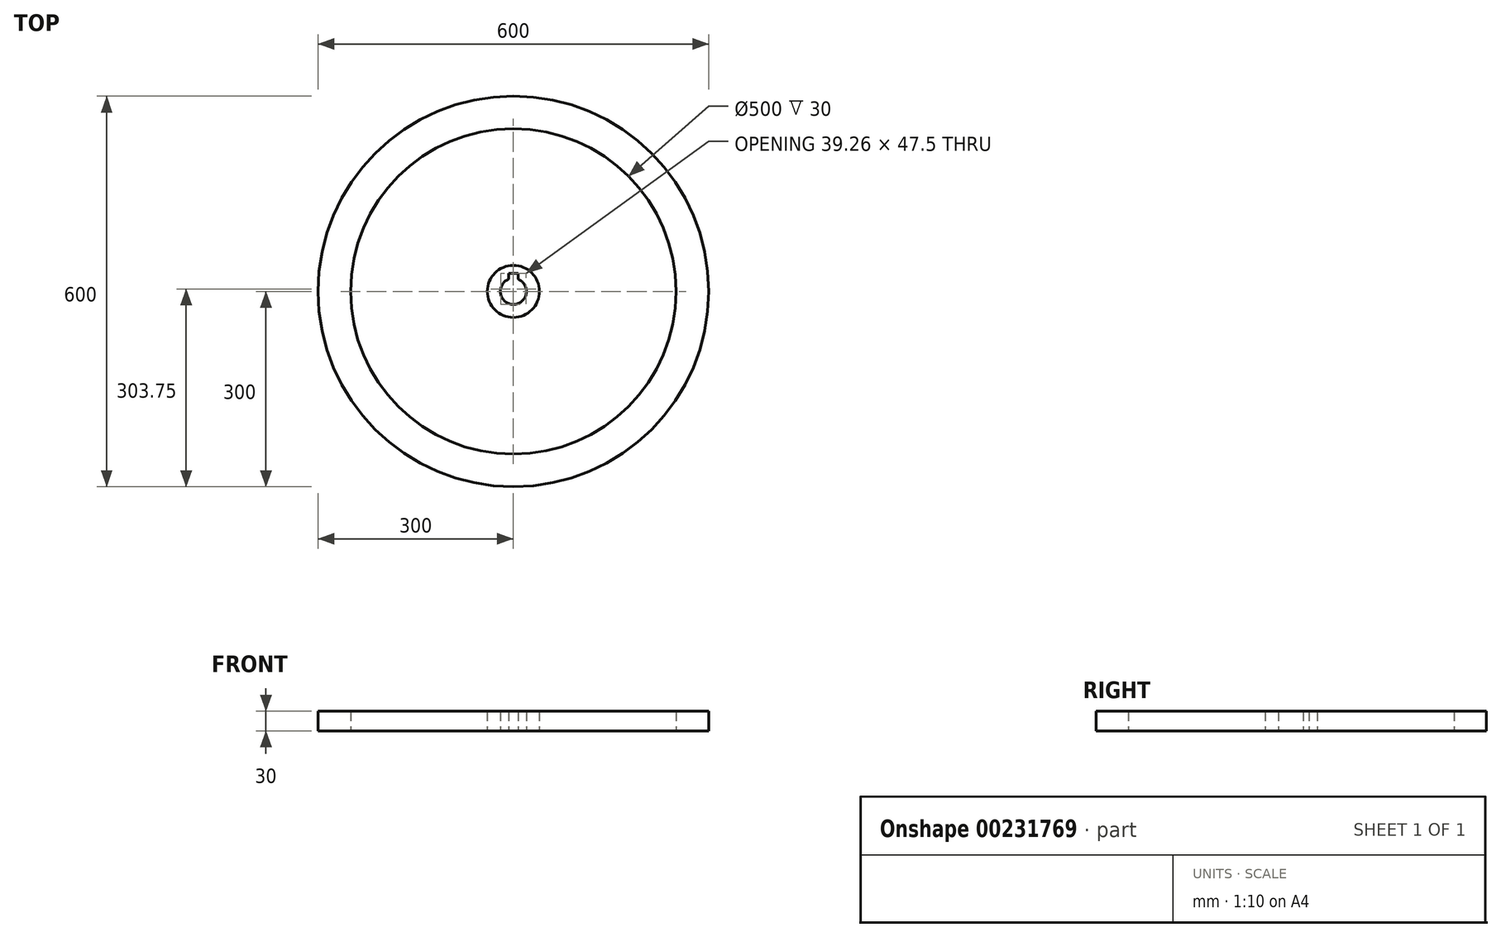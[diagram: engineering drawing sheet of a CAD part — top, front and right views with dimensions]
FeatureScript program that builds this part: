
annotation { "Feature Type Name" : "Feature", "Feature Type Description" : "" }
export const myFeature = defineFeature(function(context is Context, id is Id, definition is map)
    precondition{}
    {
        {
            var Q0;
            Q0=qCreatedBy(makeId("Top.planeOp"),FACE);
            var sketch = newSketch(context, id + "F0", { "sketchPlane" : qUnion([Q0])});
            skArc(sketch, "E0", {"start": v(-7.5, 18.54) * mm, "mid": v(0, -20) * mm, "end": v(7.5, 18.54) * mm});
            skLineSegment(sketch, "E1", {"start": v(-7.5, 18.54) * mm, "end": v(-7.5, 27.5) * mm});
            skLineSegment(sketch, "E2", {"start": v(-7.5, 27.5) * mm, "end": v(7.5, 27.5) * mm});
            skLineSegment(sketch, "E3", {"start": v(7.5, 27.5) * mm, "end": v(7.5, 18.54) * mm});
            skCircle(sketch, "E4", {"center": v(0, 0) * mm, "radius": 40 * mm});
            skCircle(sketch, "E5", {"center": v(0, 0) * mm, "radius": 250 * mm});
            skCircle(sketch, "E6", {"center": v(0, 0) * mm, "radius": 300 * mm});
            skSolve(sketch);
        }
        {
            var Q0;
            Q0=makeQuery(id+"F0.imprint","IMPRINT",FACE,{"disambiguationData":[TD([[makeQuery(id+"F0.imprint","IMPRINT",EDGE,{"derivedFrom":sQuery(id+"F0.wireOp",EDGE,"E0")}),-1.0]])]});
            var Q1;
            Q1=makeQuery(id+"F0.imprint","IMPRINT",FACE,{"disambiguationData":[TD([[makeQuery(id+"F0.imprint","IMPRINT",EDGE,{"derivedFrom":sQuery(id+"F0.wireOp",EDGE,"E5")}),-1.0]])]});
            extrude(context, id + "F1", {"entities" : qUnion([Q0, Q1]), "depth" : 30 * mm});
        }
    });
